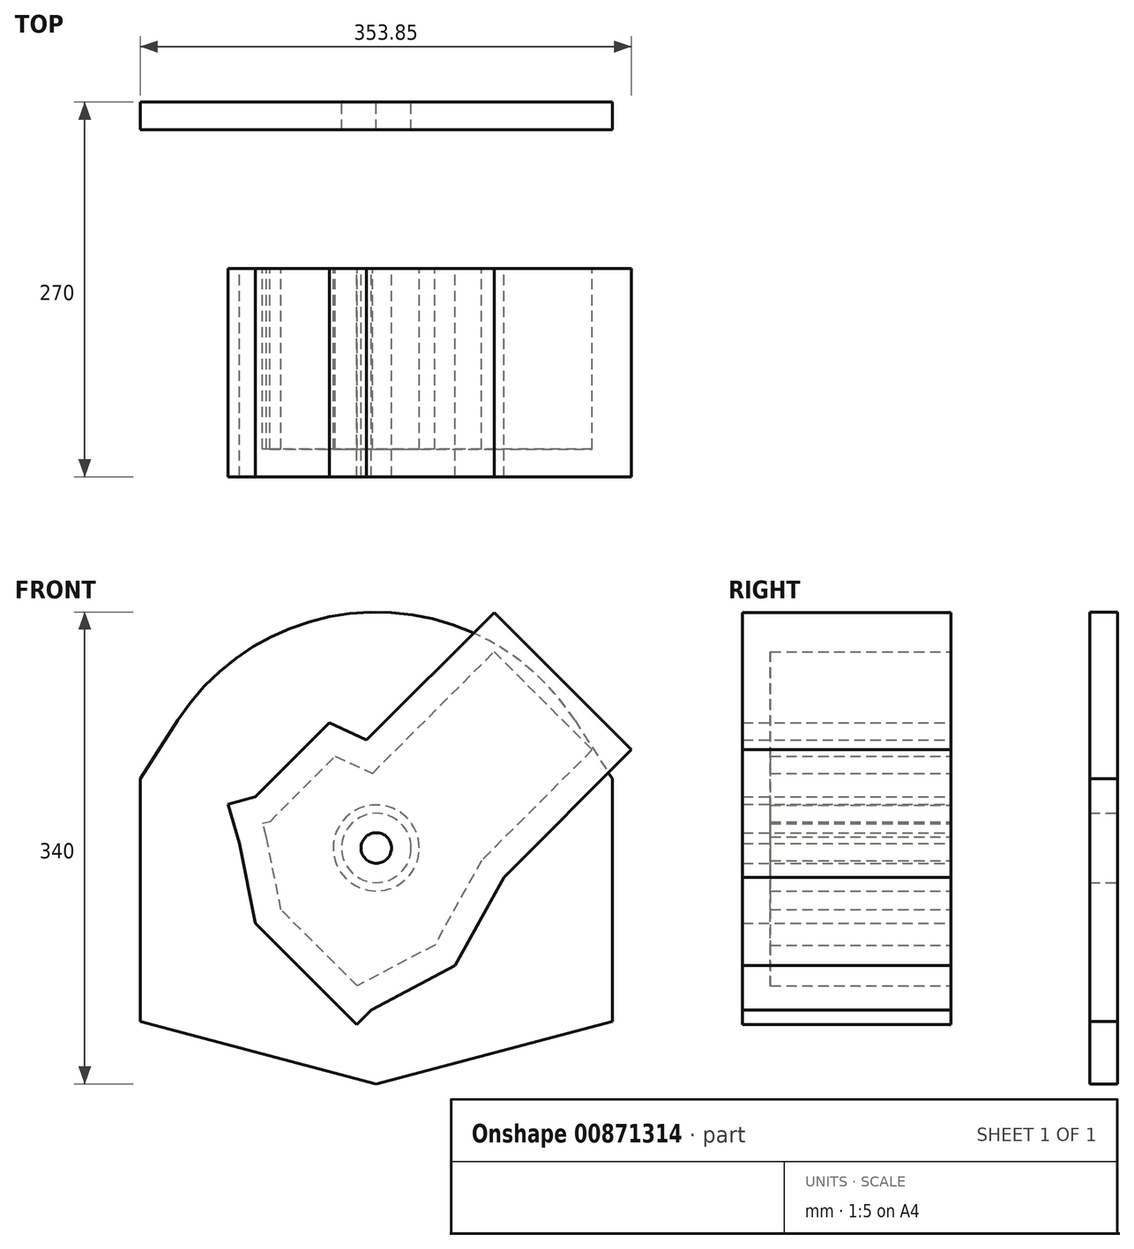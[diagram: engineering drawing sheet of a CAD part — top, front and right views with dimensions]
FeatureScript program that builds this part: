
annotation { "Feature Type Name" : "Feature", "Feature Type Description" : "" }
export const myFeature = defineFeature(function(context is Context, id is Id, definition is map)
    precondition{}
    {
        {
            var Q0;
            Q0=qCreatedBy(makeId("Right.planeOp"),FACE);
            var sketch = newSketch(context, id + "F0", { "sketchPlane" : qUnion([Q0])});
            skLineSegment(sketch, "E0", {"start": v(-322, 0) * mm, "end": v(1678, 0) * mm, "construction": true});
            skSolve(sketch);
        }
        {
            var Q0;
            Q0=qCreatedBy(makeId("Front.planeOp"),FACE);
            var sketch = newSketch(context, id + "F1", { "sketchPlane" : qUnion([Q0])});
            skLineSegment(sketch, "E1", {"start": v(170, 50) * mm, "end": v(170, -125) * mm});
            skLineSegment(sketch, "E2", {"start": v(170, -125) * mm, "end": v(0, -170) * mm});
            skLineSegment(sketch, "E3", {"start": v(0, -170) * mm, "end": v(-170, -125) * mm});
            skLineSegment(sketch, "E4", {"start": v(-170, -125) * mm, "end": v(-170, 50) * mm});
            skLineSegment(sketch, "E5", {"start": v(-170, 50) * mm, "end": v(-142.93, 92.04) * mm});
            skLineSegment(sketch, "E6", {"start": v(142.93, 92.04) * mm, "end": v(170, 50) * mm});
            skPoint(sketch, "E7.visualSharp", {"position": v(0, 314) * mm});
            skArc(sketch, "E7.filletArc", {"start": v(142.93, 92.04) * mm, "mid": v(0, 170) * mm, "end": v(-142.93, 92.04) * mm});
            skCircle(sketch, "E8", {"center": v(0, 0) * mm, "radius": 25 * mm});
            skSolve(sketch);
        }
        {
            var Q0;
            Q0 = qSketchRegion(id + "F1", true);
            extrude(context, id + "F2", {"entities" : qUnion([Q0]), "depth" : 20 * mm, "offsetDistance" : 25 * mm});
        }
        {
            var Q0;
            Q0=qCreatedBy(makeId("Front.planeOp"),FACE);
            var sketch = newSketch(context, id + "F3", { "sketchPlane" : qUnion([Q0])});
            skLineSegment(sketch, "E9", {"start": v(-60, 180) * mm, "end": v(80, 180) * mm});
            skLineSegment(sketch, "E10", {"start": v(80, 180) * mm, "end": v(80, 50) * mm});
            skLineSegment(sketch, "E11", {"start": v(80, 50) * mm, "end": v(100, -20) * mm});
            skLineSegment(sketch, "E12", {"start": v(100, -20) * mm, "end": v(80, -85) * mm});
            skLineSegment(sketch, "E13", {"start": v(80, -85) * mm, "end": v(80, -100) * mm});
            skLineSegment(sketch, "E14", {"start": v(80, -100) * mm, "end": v(-23.1, -100) * mm});
            skLineSegment(sketch, "E15", {"start": v(-23.1, -100) * mm, "end": v(-72.03, -67.41) * mm});
            skLineSegment(sketch, "E16", {"start": v(-72.03, -67.41) * mm, "end": v(-97.84, -53.12) * mm});
            skLineSegment(sketch, "E17", {"start": v(-87.67, -35.54) * mm, "end": v(-97.84, -53.12) * mm});
            skLineSegment(sketch, "E18", {"start": v(-87.67, -35.54) * mm, "end": v(-87.67, 39.8) * mm});
            skLineSegment(sketch, "E19", {"start": v(-87.67, 39.8) * mm, "end": v(-60, 50) * mm});
            skLineSegment(sketch, "E20", {"start": v(-60, 50) * mm, "end": v(-60, 180) * mm});
            skCircle(sketch, "E21", {"center": v(0, 0) * mm, "radius": 11 * mm});
            skSolve(sketch);
        }
        {
            var Q0;
            Q0 = qSketchRegion(id + "F3", true);
            extrude(context, id + "F4", {"entities" : qUnion([Q0]), "depth" : 150 * mm, "offsetDistance" : 25 * mm});
        }
        {
            var Q0;
            Q0=makeQuery(id+"F4.opExtrude","CAP_FACE",FACE,{"disambiguationData":[OSD([sQuery(id+"F3.wireOp",EDGE,"E9"),sQuery(id+"F3.wireOp",EDGE,"E10"),sQuery(id+"F3.wireOp",EDGE,"E11"),sQuery(id+"F3.wireOp",EDGE,"E12"),sQuery(id+"F3.wireOp",EDGE,"E13"),sQuery(id+"F3.wireOp",EDGE,"E14"),sQuery(id+"F3.wireOp",EDGE,"E15"),sQuery(id+"F3.wireOp",EDGE,"E16"),sQuery(id+"F3.wireOp",EDGE,"E17"),sQuery(id+"F3.wireOp",EDGE,"E18"),sQuery(id+"F3.wireOp",EDGE,"E19"),sQuery(id+"F3.wireOp",EDGE,"E20"),sQuery(id+"F3.wireOp",EDGE,"E21")])],"isStart":true});
            shell(context, id + "F5", {"entities" : qUnion([Q0]), "thickness" : 20 * mm});
        }
        {
            var Q0;
            Q0=makeQuery(id+"F4.opExtrude","SWEPT_BODY",BODY,{"disambiguationData":[OSD([sQuery(id+"F3.wireOp",EDGE,"E9"),sQuery(id+"F3.wireOp",EDGE,"E10"),sQuery(id+"F3.wireOp",EDGE,"E11"),sQuery(id+"F3.wireOp",EDGE,"E12"),sQuery(id+"F3.wireOp",EDGE,"E13"),sQuery(id+"F3.wireOp",EDGE,"E14"),sQuery(id+"F3.wireOp",EDGE,"E15"),sQuery(id+"F3.wireOp",EDGE,"E16"),sQuery(id+"F3.wireOp",EDGE,"E17"),sQuery(id+"F3.wireOp",EDGE,"E18"),sQuery(id+"F3.wireOp",EDGE,"E19"),sQuery(id+"F3.wireOp",EDGE,"E20"),sQuery(id+"F3.wireOp",EDGE,"E21")])]});
            var Q1;
            Q1=makeQuery(id+"F4.opExtrude","CAP_EDGE",EDGE,{"disambiguationData":[OSD([sQuery(id+"F3.wireOp",EDGE,"E21")])],"isStart":false});
            transform(context, id + "F6", {"entities" : qUnion([Q0]), "transformType" : TransformType.ROTATION, "transformAxis" : qUnion([Q1]), "angle" : 315 * degree, "makeCopy" : false});
        }
        {
            var Q0;
            Q0=makeQuery(id+"F4.opExtrude","SWEPT_BODY",BODY,{"disambiguationData":[OSD([sQuery(id+"F3.wireOp",EDGE,"E9"),sQuery(id+"F3.wireOp",EDGE,"E10"),sQuery(id+"F3.wireOp",EDGE,"E11"),sQuery(id+"F3.wireOp",EDGE,"E12"),sQuery(id+"F3.wireOp",EDGE,"E13"),sQuery(id+"F3.wireOp",EDGE,"E14"),sQuery(id+"F3.wireOp",EDGE,"E15"),sQuery(id+"F3.wireOp",EDGE,"E16"),sQuery(id+"F3.wireOp",EDGE,"E17"),sQuery(id+"F3.wireOp",EDGE,"E18"),sQuery(id+"F3.wireOp",EDGE,"E19"),sQuery(id+"F3.wireOp",EDGE,"E20"),sQuery(id+"F3.wireOp",EDGE,"E21")])]});
            transform(context, id + "F7", {"entities" : qUnion([Q0]), "transformType" : TransformType.TRANSLATION_3D, "dx" : 0 * mm, "dy" : -120 * mm, "dz" : 0 * mm, "makeCopy" : false});
        }
        {
            var Q0;
            Q0=qCreatedBy(makeId("Right.planeOp"),FACE);
            var sketch = newSketch(context, id + "F8", { "sketchPlane" : qUnion([Q0])});
            skLineSegment(sketch, "E22", {"start": v(0, -170) * mm, "end": v(125, -192.04) * mm});
            skLineSegment(sketch, "E23", {"start": v(275, -192.04) * mm, "end": v(1678, 0) * mm});
            skLineSegment(sketch, "E24", {"start": v(1678, 0) * mm, "end": v(1678, 50) * mm});
            skLineSegment(sketch, "E25", {"start": v(546.2, 217.87) * mm, "end": v(87.96, 257.96) * mm});
            skLineSegment(sketch, "E26", {"start": v(87.96, 257.96) * mm, "end": v(0, 170) * mm});
            skLineSegment(sketch, "E27", {"start": v(0, 170) * mm, "end": v(0, -170) * mm});
            skLineSegment(sketch, "E28", {"start": v(125, -192.04) * mm, "end": v(275, -192.04) * mm});
            skLineSegment(sketch, "E29", {"start": v(546.2, 217.87) * mm, "end": v(1678, 50) * mm});
            skSolve(sketch);
        }
    });
